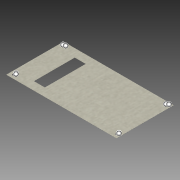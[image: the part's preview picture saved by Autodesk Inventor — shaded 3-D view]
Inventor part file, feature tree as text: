
AUTODESK INVENTOR PART (.ipt)
format: ipt  version: 2015 (Build 190159000, 159)  size: 126,464 bytes
history: native  units: mm
features: sketch x3, extrude x2, projected_geometry x2, hole x1
ambient origin geometry x8: Origin, YZ Plane, XZ Plane, XY Plane, X Axis, Y Axis, Z Axis, Center Point
bodies: Solid1 (feature_tree)
feature tree (8):
  extrude  "Extrusion1"  Depth=75.9mm
  hole  "Hole1"  [1 undecoded]
  extrude  "Extrusion2"  TaperAngle=0.0deg  [1 undecoded]
  sketch  "Sketch1"  dims[d0=145.9mm d1=75.9mm]
  sketch  "Sketch2"  dims[d2=0.1mm d3=0.0mm d4=4.85mm]
  projected_geometry  "Projected Loop1"
  sketch  "Sketch3"  dims[d5=3.0mm d6=6.0mm d7=4.0mm d8=2.0mm d9=90.0deg d10=8.0mm d11=20.594885mm d12=0.0mm d13=0.0mm d14=0.0mm d15=0.0mm d16=0.0mm d17=0.0mm d18=0.0mm d19=0.0mm d20=105.7mm d21=14.4mm d22=54.0mm d23=10.95mm d24=0.1mm d25=0.0mm]
  projected_geometry  "Projected Loop2"
note: 2 required parameter values undecoded (feature->parameter linkage not recoverable at this tier; creation-order binding heuristic only, values carry confidence <= 0.55)
